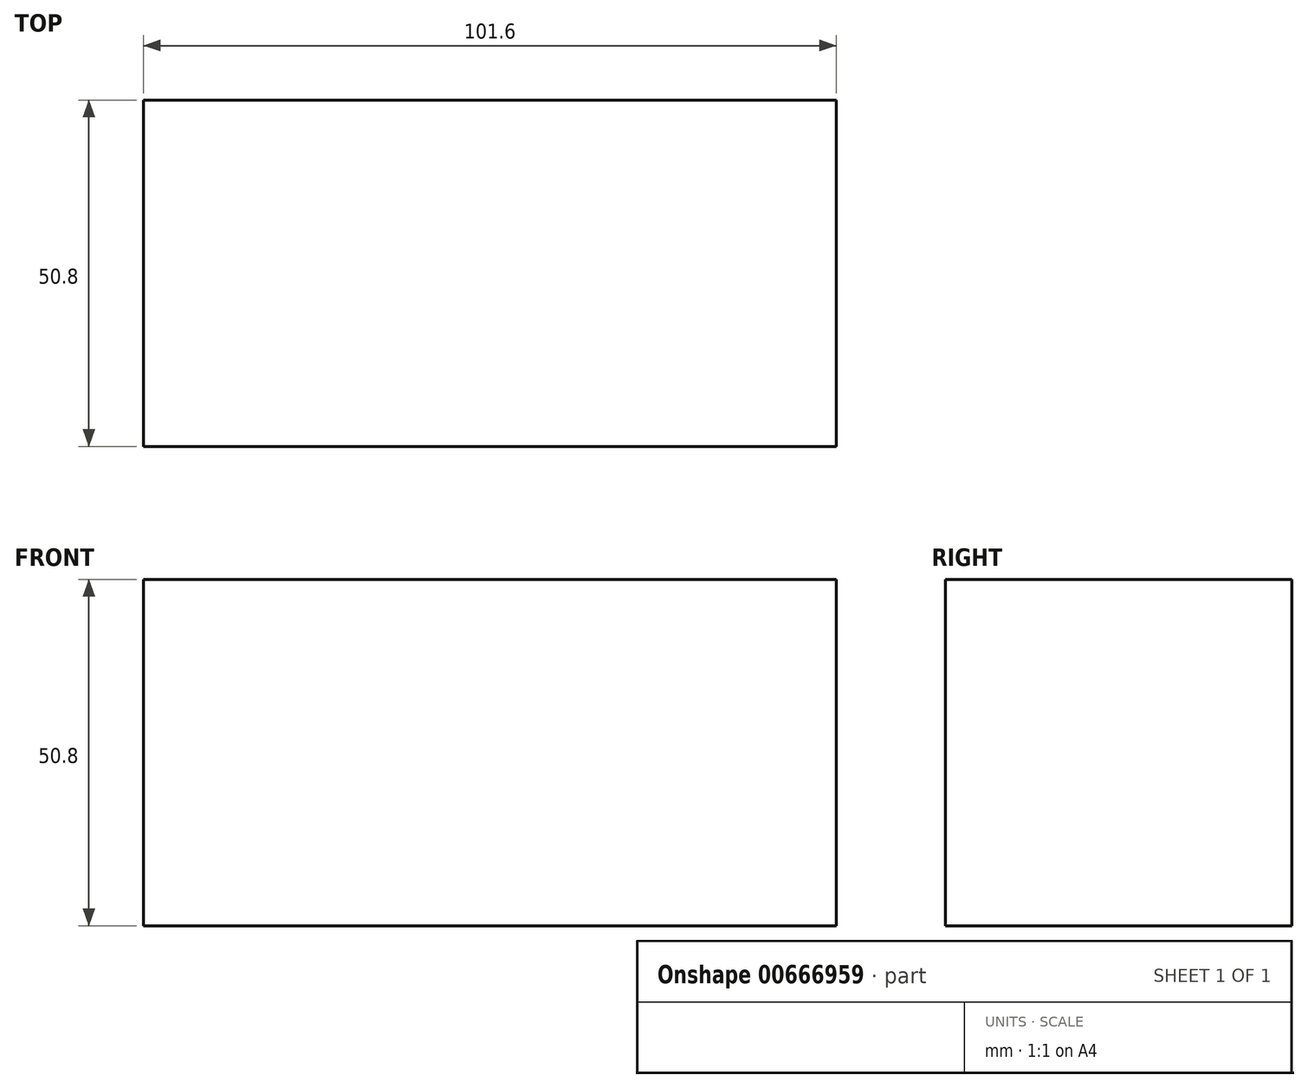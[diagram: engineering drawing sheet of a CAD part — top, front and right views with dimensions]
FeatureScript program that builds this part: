
annotation { "Feature Type Name" : "Feature", "Feature Type Description" : "" }
export const myFeature = defineFeature(function(context is Context, id is Id, definition is map)
    precondition{}
    {
        {
            var Q0;
            Q0=qCreatedBy(makeId("Front.planeOp"),FACE);
            var sketch = newSketch(context, id + "F0", { "sketchPlane" : qUnion([Q0])});
            skLineSegment(sketch, "E0.bottom", {"start": v(0, 0) * mm, "end": v(101.6, 0) * mm});
            skLineSegment(sketch, "E0.top", {"start": v(0, 50.8) * mm, "end": v(101.6, 50.8) * mm});
            skLineSegment(sketch, "E0.left", {"start": v(0, 0) * mm, "end": v(0, 50.8) * mm});
            skLineSegment(sketch, "E0.right", {"start": v(101.6, 0) * mm, "end": v(101.6, 50.8) * mm});
            skSolve(sketch);
        }
        {
            var Q0;
            Q0 = qSketchRegion(id + "F0", true);
            extrude(context, id + "F1", {"entities" : qUnion([Q0]), "depth" : 50.8 * mm, "offsetDistance" : 25.4 * mm});
        }
    });
